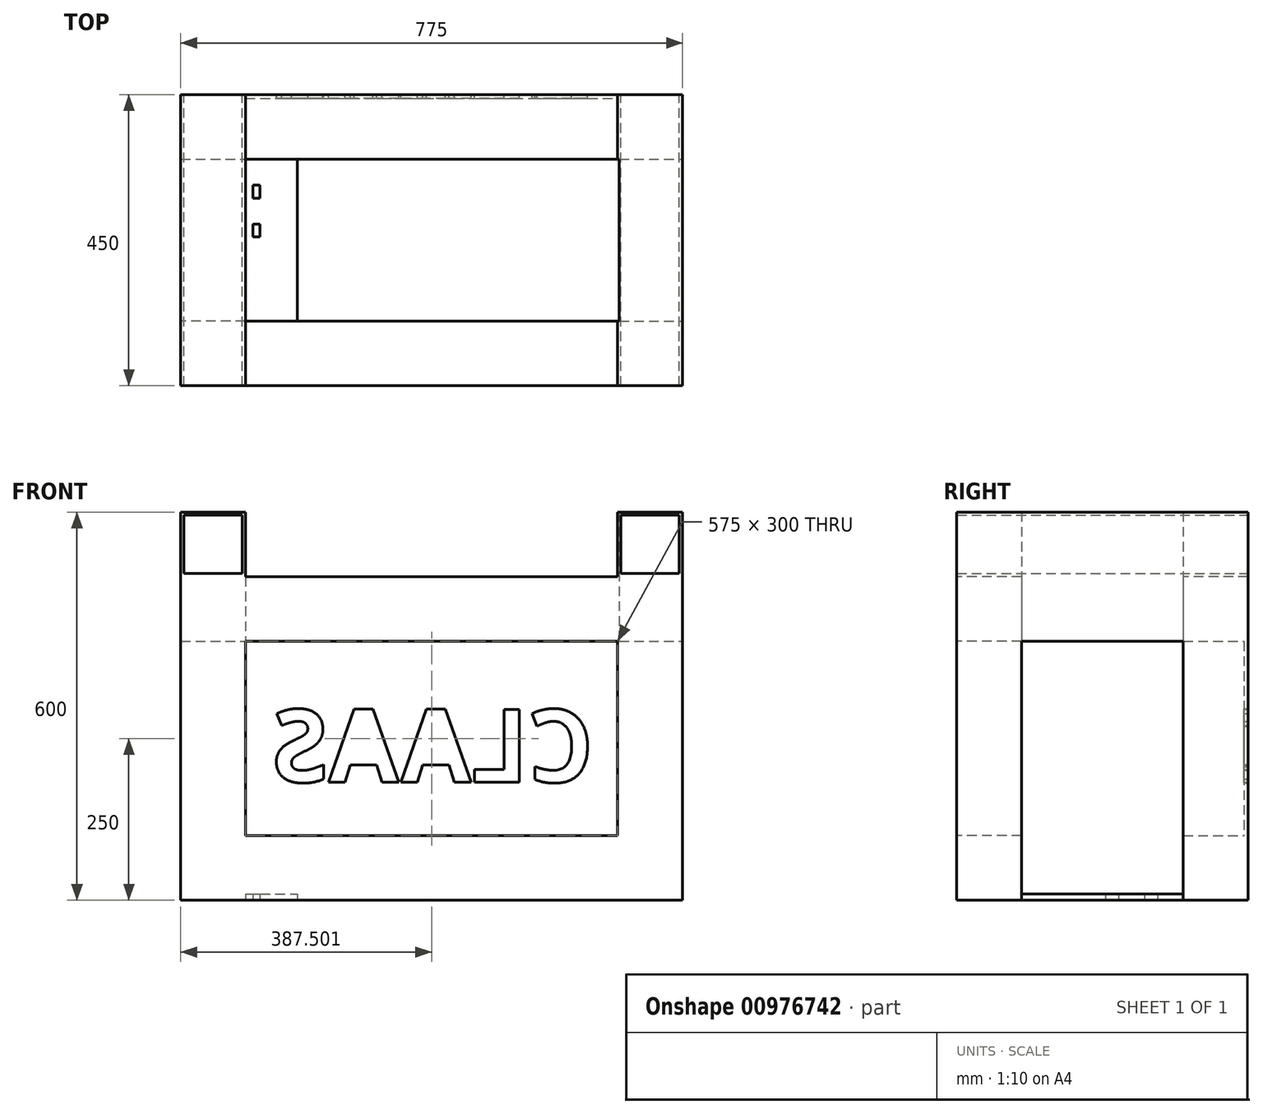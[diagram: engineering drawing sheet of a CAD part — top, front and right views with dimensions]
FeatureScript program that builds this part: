
annotation { "Feature Type Name" : "Feature", "Feature Type Description" : "" }
export const myFeature = defineFeature(function(context is Context, id is Id, definition is map)
    precondition{}
    {
        {
            var Q0;
            Q0=qCreatedBy(makeId("Top.planeOp"),FACE);
            var sketch = newSketch(context, id + "F0", { "sketchPlane" : qUnion([Q0])});
            skLineSegment(sketch, "E0.bottom", {"start": v(-50.26, -160.16) * mm, "end": v(724.74, -160.16) * mm});
            skLineSegment(sketch, "E0.top", {"start": v(-50.26, -260.16) * mm, "end": v(724.74, -260.16) * mm});
            skLineSegment(sketch, "E0.left", {"start": v(-50.26, -160.16) * mm, "end": v(-50.26, -260.16) * mm});
            skLineSegment(sketch, "E0.right", {"start": v(724.74, -160.16) * mm, "end": v(724.74, -260.16) * mm});
            skLineSegment(sketch, "E1.bottom", {"start": v(-50.26, -260.16) * mm, "end": v(49.74, -260.16) * mm});
            skLineSegment(sketch, "E1.top", {"start": v(-50.26, -510.16) * mm, "end": v(49.74, -510.16) * mm});
            skLineSegment(sketch, "E1.left", {"start": v(-50.26, -260.16) * mm, "end": v(-50.26, -510.16) * mm});
            skLineSegment(sketch, "E1.right", {"start": v(49.74, -260.16) * mm, "end": v(49.74, -510.16) * mm});
            skLineSegment(sketch, "E2.bottom", {"start": v(724.74, -260.16) * mm, "end": v(624.74, -260.16) * mm});
            skLineSegment(sketch, "E2.top", {"start": v(724.74, -510.16) * mm, "end": v(624.74, -510.16) * mm});
            skLineSegment(sketch, "E2.left", {"start": v(724.74, -260.16) * mm, "end": v(724.74, -510.16) * mm});
            skLineSegment(sketch, "E2.right", {"start": v(624.74, -260.16) * mm, "end": v(624.74, -510.16) * mm});
            skLineSegment(sketch, "E3.bottom", {"start": v(-50.26, -510.16) * mm, "end": v(724.74, -510.16) * mm});
            skLineSegment(sketch, "E3.top", {"start": v(-50.26, -610.16) * mm, "end": v(724.74, -610.16) * mm});
            skLineSegment(sketch, "E3.left", {"start": v(-50.26, -510.16) * mm, "end": v(-50.26, -610.16) * mm});
            skLineSegment(sketch, "E3.right", {"start": v(724.74, -510.16) * mm, "end": v(724.74, -610.16) * mm});
            skSolve(sketch);
        }
        {
            var Q0;
            Q0=makeQuery(id+"F0.imprint","IMPRINT",FACE,{"disambiguationData":[TD([[makeQuery(id+"F0.imprint","IMPRINT",EDGE,{"derivedFrom":sQuery(id+"F0.wireOp",EDGE,"E0.bottom")}),-1.0]])]});
            var Q1;
            Q1=makeQuery(id+"F0.imprint","IMPRINT",FACE,{"disambiguationData":[TD([[makeQuery(id+"F0.imprint","IMPRINT",EDGE,{"derivedFrom":sQuery(id+"F0.wireOp",EDGE,"E1.bottom")}),-1.0]])]});
            var Q2;
            Q2=makeQuery(id+"F0.imprint","IMPRINT",FACE,{"disambiguationData":[TD([[makeQuery(id+"F0.imprint","IMPRINT",EDGE,{"derivedFrom":sQuery(id+"F0.wireOp",EDGE,"E2.bottom")}),1.0]])]});
            var Q3;
            Q3=makeQuery(id+"F0.imprint","IMPRINT",FACE,{"disambiguationData":[TD([[makeQuery(id+"F0.imprint","IMPRINT",EDGE,{"derivedFrom":sQuery(id+"F0.wireOp",EDGE,"E3.top")}),1.0]])]});
            extrude(context, id + "F1", {"entities" : qUnion([Q0, Q1, Q2, Q3]), "depth" : 100 * mm, "offsetDistance" : 25 * mm});
        }
        {
            var Q0;
            Q0=makeQuery(id+"F1.opExtrude","CAP_FACE",FACE,{"disambiguationData":[OSD([sQuery(id+"F0.wireOp",EDGE,"E0.bottom"),sQuery(id+"F0.wireOp",EDGE,"E0.top"),sQuery(id+"F0.wireOp",EDGE,"E0.left"),sQuery(id+"F0.wireOp",EDGE,"E0.right"),sQuery(id+"F0.wireOp",EDGE,"E1.left"),sQuery(id+"F0.wireOp",EDGE,"E1.right"),sQuery(id+"F0.wireOp",EDGE,"E2.left"),sQuery(id+"F0.wireOp",EDGE,"E2.right"),sQuery(id+"F0.wireOp",EDGE,"E3.bottom"),sQuery(id+"F0.wireOp",EDGE,"E3.top"),sQuery(id+"F0.wireOp",EDGE,"E3.left"),sQuery(id+"F0.wireOp",EDGE,"E3.right")])],"isStart":false});
            var sketch = newSketch(context, id + "F2", { "sketchPlane" : qUnion([Q0])});
            skLineSegment(sketch, "E4.bottom", {"start": v(-50.26, -160.16) * mm, "end": v(49.74, -160.16) * mm});
            skLineSegment(sketch, "E4.top", {"start": v(-50.26, -260.16) * mm, "end": v(49.74, -260.16) * mm});
            skLineSegment(sketch, "E4.left", {"start": v(-50.26, -160.16) * mm, "end": v(-50.26, -260.16) * mm});
            skLineSegment(sketch, "E4.right", {"start": v(49.74, -160.16) * mm, "end": v(49.74, -260.16) * mm});
            skLineSegment(sketch, "E5.bottom", {"start": v(624.74, -260.16) * mm, "end": v(724.74, -260.16) * mm});
            skLineSegment(sketch, "E5.top", {"start": v(624.74, -160.16) * mm, "end": v(724.74, -160.16) * mm});
            skLineSegment(sketch, "E5.left", {"start": v(624.74, -260.16) * mm, "end": v(624.74, -160.16) * mm});
            skLineSegment(sketch, "E5.right", {"start": v(724.74, -260.16) * mm, "end": v(724.74, -160.16) * mm});
            skLineSegment(sketch, "E6.bottom", {"start": v(624.74, -510.16) * mm, "end": v(724.74, -510.16) * mm});
            skLineSegment(sketch, "E6.top", {"start": v(624.74, -610.16) * mm, "end": v(724.74, -610.16) * mm});
            skLineSegment(sketch, "E6.left", {"start": v(624.74, -510.16) * mm, "end": v(624.74, -610.16) * mm});
            skLineSegment(sketch, "E6.right", {"start": v(724.74, -510.16) * mm, "end": v(724.74, -610.16) * mm});
            skLineSegment(sketch, "E7.bottom", {"start": v(49.74, -510.16) * mm, "end": v(-50.26, -510.16) * mm});
            skLineSegment(sketch, "E7.top", {"start": v(49.74, -610.16) * mm, "end": v(-50.26, -610.16) * mm});
            skLineSegment(sketch, "E7.left", {"start": v(49.74, -510.16) * mm, "end": v(49.74, -610.16) * mm});
            skLineSegment(sketch, "E7.right", {"start": v(-50.26, -510.16) * mm, "end": v(-50.26, -610.16) * mm});
            skSolve(sketch);
        }
        {
            var Q0;
            Q0=makeQuery(id+"F2.imprint","IMPRINT",FACE,{"disambiguationData":[TD([[makeQuery(id+"F2.imprint","IMPRINT",EDGE,{"derivedFrom":sQuery(id+"F2.wireOp",EDGE,"E4.bottom")}),-1.0]])]});
            var Q1;
            Q1=makeQuery(id+"F2.imprint","IMPRINT",FACE,{"disambiguationData":[TD([[makeQuery(id+"F2.imprint","IMPRINT",EDGE,{"derivedFrom":sQuery(id+"F2.wireOp",EDGE,"E5.bottom")}),1.0]])]});
            var Q2;
            Q2=makeQuery(id+"F2.imprint","IMPRINT",FACE,{"disambiguationData":[TD([[makeQuery(id+"F2.imprint","IMPRINT",EDGE,{"derivedFrom":sQuery(id+"F2.wireOp",EDGE,"E6.bottom")}),-1.0]])]});
            var Q3;
            Q3=makeQuery(id+"F2.imprint","IMPRINT",FACE,{"disambiguationData":[TD([[makeQuery(id+"F2.imprint","IMPRINT",EDGE,{"derivedFrom":sQuery(id+"F2.wireOp",EDGE,"E7.bottom")}),1.0]])]});
            extrude(context, id + "F3", {"entities" : qUnion([Q0, Q1, Q2, Q3]), "operationType" : NewBodyOperationType.ADD, "depth" : 300 * mm, "offsetDistance" : 25 * mm});
        }
        {
            var Q0;
            Q0=makeQuery(id+"F3.opExtrude","CAP_FACE",FACE,{"disambiguationData":[OSD([sQuery(id+"F2.wireOp",EDGE,"E4.bottom"),sQuery(id+"F2.wireOp",EDGE,"E4.top"),sQuery(id+"F2.wireOp",EDGE,"E4.left"),sQuery(id+"F2.wireOp",EDGE,"E4.right")])],"isStart":false});
            var sketch = newSketch(context, id + "F4", { "sketchPlane" : qUnion([Q0])});
            skLineSegment(sketch, "E8.bottom", {"start": v(-50.26, -160.16) * mm, "end": v(724.74, -160.16) * mm});
            skLineSegment(sketch, "E8.top", {"start": v(-50.26, -260.16) * mm, "end": v(724.74, -260.16) * mm});
            skLineSegment(sketch, "E8.left", {"start": v(-50.26, -160.16) * mm, "end": v(-50.26, -260.16) * mm});
            skLineSegment(sketch, "E8.right", {"start": v(724.74, -160.16) * mm, "end": v(724.74, -260.16) * mm});
            skLineSegment(sketch, "E9.bottom", {"start": v(724.74, -260.16) * mm, "end": v(627.24, -260.16) * mm});
            skLineSegment(sketch, "E9.top", {"start": v(724.74, -510.16) * mm, "end": v(627.24, -510.16) * mm});
            skLineSegment(sketch, "E9.left", {"start": v(724.74, -260.16) * mm, "end": v(724.74, -510.16) * mm});
            skLineSegment(sketch, "E9.right", {"start": v(627.24, -260.16) * mm, "end": v(627.24, -510.16) * mm});
            skLineSegment(sketch, "E10.bottom", {"start": v(724.74, -510.16) * mm, "end": v(-50.26, -510.16) * mm});
            skLineSegment(sketch, "E10.top", {"start": v(724.74, -610.16) * mm, "end": v(-50.26, -610.16) * mm});
            skLineSegment(sketch, "E10.left", {"start": v(724.74, -510.16) * mm, "end": v(724.74, -610.16) * mm});
            skLineSegment(sketch, "E10.right", {"start": v(-50.26, -510.16) * mm, "end": v(-50.26, -610.16) * mm});
            skLineSegment(sketch, "E11.bottom", {"start": v(-50.26, -510.16) * mm, "end": v(49.74, -510.16) * mm});
            skLineSegment(sketch, "E11.top", {"start": v(-50.26, -260.16) * mm, "end": v(49.74, -260.16) * mm});
            skLineSegment(sketch, "E11.left", {"start": v(-50.26, -510.16) * mm, "end": v(-50.26, -260.16) * mm});
            skLineSegment(sketch, "E11.right", {"start": v(49.74, -510.16) * mm, "end": v(49.74, -260.16) * mm});
            skSolve(sketch);
        }
        {
            var Q0;
            Q0 = qSketchRegion(id + "F4", true);
            extrude(context, id + "F5", {"entities" : qUnion([Q0]), "operationType" : NewBodyOperationType.ADD, "depth" : 100 * mm, "offsetDistance" : 25 * mm});
        }
        {
            var Q0;
            Q0=makeQuery(id+"F1.opExtrude","CAP_FACE",FACE,{"disambiguationData":[OSD([sQuery(id+"F0.wireOp",EDGE,"E0.bottom"),sQuery(id+"F0.wireOp",EDGE,"E0.top"),sQuery(id+"F0.wireOp",EDGE,"E0.left"),sQuery(id+"F0.wireOp",EDGE,"E0.right"),sQuery(id+"F0.wireOp",EDGE,"E1.left"),sQuery(id+"F0.wireOp",EDGE,"E1.right"),sQuery(id+"F0.wireOp",EDGE,"E2.left"),sQuery(id+"F0.wireOp",EDGE,"E2.right"),sQuery(id+"F0.wireOp",EDGE,"E3.bottom"),sQuery(id+"F0.wireOp",EDGE,"E3.top"),sQuery(id+"F0.wireOp",EDGE,"E3.left"),sQuery(id+"F0.wireOp",EDGE,"E3.right")])],"isStart":true});
            var sketch = newSketch(context, id + "F6", { "sketchPlane" : qUnion([Q0])});
            skLineSegment(sketch, "E12.bottom", {"start": v(49.74, 510.16) * mm, "end": v(129.74, 510.16) * mm});
            skLineSegment(sketch, "E12.top", {"start": v(49.74, 260.16) * mm, "end": v(129.74, 260.16) * mm});
            skLineSegment(sketch, "E12.left", {"start": v(49.74, 510.16) * mm, "end": v(49.74, 260.16) * mm});
            skLineSegment(sketch, "E12.right", {"start": v(129.74, 510.16) * mm, "end": v(129.74, 260.16) * mm});
            skLineSegment(sketch, "E13.bottom", {"start": v(624.74, 510.16) * mm, "end": v(544.74, 510.16) * mm});
            skLineSegment(sketch, "E13.top", {"start": v(624.74, 260.16) * mm, "end": v(544.74, 260.16) * mm});
            skLineSegment(sketch, "E13.left", {"start": v(624.74, 510.16) * mm, "end": v(624.74, 260.16) * mm});
            skLineSegment(sketch, "E13.right", {"start": v(544.74, 510.16) * mm, "end": v(544.74, 260.16) * mm});
            skLineSegment(sketch, "E14.bottom", {"start": v(61.24, 300.16) * mm, "end": v(72.24, 300.16) * mm});
            skLineSegment(sketch, "E14.top", {"start": v(61.24, 320.16) * mm, "end": v(72.24, 320.16) * mm});
            skLineSegment(sketch, "E14.left", {"start": v(61.24, 300.16) * mm, "end": v(61.24, 320.16) * mm});
            skLineSegment(sketch, "E14.right", {"start": v(72.24, 300.16) * mm, "end": v(72.24, 320.16) * mm});
            skLineSegment(sketch, "E15.bottom", {"start": v(61.24, 360.16) * mm, "end": v(72.24, 360.16) * mm});
            skLineSegment(sketch, "E15.top", {"start": v(61.24, 380.16) * mm, "end": v(72.24, 380.16) * mm});
            skLineSegment(sketch, "E15.left", {"start": v(61.24, 360.16) * mm, "end": v(61.24, 380.16) * mm});
            skLineSegment(sketch, "E15.right", {"start": v(72.24, 360.16) * mm, "end": v(72.24, 380.16) * mm});
            skLineSegment(sketch, "E16.bottom", {"start": v(602.24, 380.16) * mm, "end": v(613.24, 380.16) * mm});
            skLineSegment(sketch, "E16.top", {"start": v(602.24, 360.16) * mm, "end": v(613.24, 360.16) * mm});
            skLineSegment(sketch, "E16.left", {"start": v(602.24, 380.16) * mm, "end": v(602.24, 360.16) * mm});
            skLineSegment(sketch, "E16.right", {"start": v(613.24, 380.16) * mm, "end": v(613.24, 360.16) * mm});
            skLineSegment(sketch, "E17.bottom", {"start": v(602.24, 320.16) * mm, "end": v(613.24, 320.16) * mm});
            skLineSegment(sketch, "E17.top", {"start": v(602.24, 300.16) * mm, "end": v(613.24, 300.16) * mm});
            skLineSegment(sketch, "E17.left", {"start": v(602.24, 320.16) * mm, "end": v(602.24, 300.16) * mm});
            skLineSegment(sketch, "E17.right", {"start": v(613.24, 320.16) * mm, "end": v(613.24, 300.16) * mm});
            skSolve(sketch);
        }
        {
            var Q0;
            Q0=makeQuery(id+"F6.imprint","IMPRINT",FACE,{"disambiguationData":[TD([[makeQuery(id+"F6.imprint","IMPRINT",EDGE,{"derivedFrom":sQuery(id+"F6.wireOp",EDGE,"E12.bottom")}),-1.0]])]});
            var Q1;
            Q1=makeQuery(id+"F6.imprint","IMPRINT",FACE,{"disambiguationData":[TD([[makeQuery(id+"F6.imprint","IMPRINT",EDGE,{"derivedFrom":sQuery(id+"F6.wireOp",EDGE,"E13.bottom")}),-1.0]])]});
            extrude(context, id + "F7", {"entities" : qUnion([Q0, Q1]), "oppositeDirection" : true, "depth" : 10 * mm, "offsetDistance" : 25 * mm});
        }
        {
            var Q0;
            Q0=makeQuery(id+"F5.boolean.opBoolean","MERGE",FACE,{"derivedFrom":[makeQuery(id+"F3.boolean.opBoolean","MERGE",FACE,{"derivedFrom":[makeQuery(id+"F1.opExtrude","SWEPT_FACE",FACE,{"disambiguationData":[OSD([sQuery(id+"F0.wireOp",EDGE,"E0.bottom")])]}),makeQuery(id+"F3.opExtrude","SWEPT_FACE",FACE,{"disambiguationData":[OSD([sQuery(id+"F2.wireOp",EDGE,"E4.bottom")])]}),makeQuery(id+"F3.opExtrude","SWEPT_FACE",FACE,{"disambiguationData":[OSD([sQuery(id+"F2.wireOp",EDGE,"E5.top")])]})]}),makeQuery(id+"F5.opExtrude","SWEPT_FACE",FACE,{"disambiguationData":[OSD([sQuery(id+"F4.wireOp",EDGE,"E8.bottom")])]})]});
            var sketch = newSketch(context, id + "F8", { "sketchPlane" : qUnion([Q0])});
            skLineSegment(sketch, "E18.bottom", {"start": v(-49.74, 100) * mm, "end": v(-624.74, 100) * mm});
            skLineSegment(sketch, "E18.top", {"start": v(-49.74, 400) * mm, "end": v(-624.74, 400) * mm});
            skLineSegment(sketch, "E18.left", {"start": v(-49.74, 100) * mm, "end": v(-49.74, 400) * mm});
            skLineSegment(sketch, "E18.right", {"start": v(-624.74, 100) * mm, "end": v(-624.74, 400) * mm});
            skText(sketch, "E19", { "text": "CLAAS", "fontName": "NotoSans-Bold.ttf"});
            const initialGuessF8  = {"E19": [-0.58724, 0.1825, 1, 0, 0.11322]};
            skSetInitialGuess(sketch, initialGuessF8);
            skSolve(sketch);
        }
        {
            var Q0;
            Q0 = qSketchRegion(id + "F8", true);
            extrude(context, id + "F9", {"entities" : qUnion([Q0]), "operationType" : NewBodyOperationType.ADD, "oppositeDirection" : true, "depth" : 6 * mm, "offsetDistance" : 25 * mm});
        }
        {
            var Q0;
            Q0=makeQuery(id+"F5.opExtrude","CAP_FACE",FACE,{"disambiguationData":[OSD([sQuery(id+"F4.wireOp",EDGE,"E8.bottom"),sQuery(id+"F4.wireOp",EDGE,"E8.top"),sQuery(id+"F4.wireOp",EDGE,"E8.left"),sQuery(id+"F4.wireOp",EDGE,"E8.right"),sQuery(id+"F4.wireOp",EDGE,"E9.left"),sQuery(id+"F4.wireOp",EDGE,"E9.right"),sQuery(id+"F4.wireOp",EDGE,"E10.bottom"),sQuery(id+"F4.wireOp",EDGE,"E10.top"),sQuery(id+"F4.wireOp",EDGE,"E10.left"),sQuery(id+"F4.wireOp",EDGE,"E10.right"),sQuery(id+"F4.wireOp",EDGE,"E11.left"),sQuery(id+"F4.wireOp",EDGE,"E11.right")])],"isStart":false});
            var sketch = newSketch(context, id + "F10", { "sketchPlane" : qUnion([Q0])});
            skLineSegment(sketch, "E20.bottom", {"start": v(-50.26, -160.16) * mm, "end": v(49.74, -160.16) * mm});
            skLineSegment(sketch, "E20.top", {"start": v(-50.26, -610.16) * mm, "end": v(49.74, -610.16) * mm});
            skLineSegment(sketch, "E20.left", {"start": v(-50.26, -160.16) * mm, "end": v(-50.26, -610.16) * mm});
            skLineSegment(sketch, "E20.right", {"start": v(49.74, -160.16) * mm, "end": v(49.74, -610.16) * mm});
            skLineSegment(sketch, "E21.bottom", {"start": v(724.74, -160.16) * mm, "end": v(624.74, -160.16) * mm});
            skLineSegment(sketch, "E21.top", {"start": v(724.74, -610.16) * mm, "end": v(624.74, -610.16) * mm});
            skLineSegment(sketch, "E21.left", {"start": v(724.74, -160.16) * mm, "end": v(724.74, -610.16) * mm});
            skLineSegment(sketch, "E21.right", {"start": v(624.74, -160.16) * mm, "end": v(624.74, -610.16) * mm});
            skSolve(sketch);
        }
        {
            var Q0;
            {var subQ2=sQuery(id+"F10.wireOp",EDGE,"E20.bottom");Q0=makeQuery(id+"F10.imprint","IMPRINT",FACE,{"disambiguationData":[TD([[makeQuery(id+"F10.imprint","IMPRINT",EDGE,{"derivedFrom":subQ2}),-1.0]])]});}
            var Q1;
            {var subQ1=sQuery(id+"F10.wireOp",EDGE,"E21.bottom");Q1=makeQuery(id+"F10.imprint","IMPRINT",FACE,{"disambiguationData":[TD([[makeQuery(id+"F10.imprint","IMPRINT",EDGE,{"derivedFrom":subQ1}),-1.0]])]});}
            extrude(context, id + "F11", {"entities" : qUnion([Q0, Q1]), "operationType" : NewBodyOperationType.ADD, "depth" : 100 * mm, "offsetDistance" : 25 * mm});
        }
        {
            var Q0;
            Q0=makeQuery(id+"F11.boolean.opBoolean","MERGE",FACE,{"derivedFrom":[makeQuery(id+"F9.boolean.opBoolean","MERGE",FACE,{"derivedFrom":[makeQuery(id+"F5.boolean.opBoolean","MERGE",FACE,{"derivedFrom":[makeQuery(id+"F3.boolean.opBoolean","MERGE",FACE,{"derivedFrom":[makeQuery(id+"F1.opExtrude","SWEPT_FACE",FACE,{"disambiguationData":[OSD([sQuery(id+"F0.wireOp",EDGE,"E0.bottom")])]}),makeQuery(id+"F3.opExtrude","SWEPT_FACE",FACE,{"disambiguationData":[OSD([sQuery(id+"F2.wireOp",EDGE,"E4.bottom")])]}),makeQuery(id+"F3.opExtrude","SWEPT_FACE",FACE,{"disambiguationData":[OSD([sQuery(id+"F2.wireOp",EDGE,"E5.top")])]})]}),makeQuery(id+"F5.opExtrude","SWEPT_FACE",FACE,{"disambiguationData":[OSD([sQuery(id+"F4.wireOp",EDGE,"E8.bottom")])]})]}),makeQuery(id+"F9.opExtrude","CAP_FACE",FACE,{"disambiguationData":[OSD([sQuery(id+"F8.wireOp",EDGE,"E18.bottom"),sQuery(id+"F8.wireOp",EDGE,"E18.top"),sQuery(id+"F8.wireOp",EDGE,"E18.left"),sQuery(id+"F8.wireOp",EDGE,"E18.right"),sQuery(id+"F8.wireOp",EDGE,"E19.sketch_text.stroke-0"),sQuery(id+"F8.wireOp",EDGE,"E19.sketch_text.stroke-1"),sQuery(id+"F8.wireOp",EDGE,"E19.sketch_text.stroke-2"),sQuery(id+"F8.wireOp",EDGE,"E19.sketch_text.stroke-3"),sQuery(id+"F8.wireOp",EDGE,"E19.sketch_text.stroke-4"),sQuery(id+"F8.wireOp",EDGE,"E19.sketch_text.stroke-5"),sQuery(id+"F8.wireOp",EDGE,"E19.sketch_text.stroke-6"),sQuery(id+"F8.wireOp",EDGE,"E19.sketch_text.stroke-7"),sQuery(id+"F8.wireOp",EDGE,"E19.sketch_text.stroke-8"),sQuery(id+"F8.wireOp",EDGE,"E19.sketch_text.stroke-9"),sQuery(id+"F8.wireOp",EDGE,"E19.sketch_text.stroke-10"),sQuery(id+"F8.wireOp",EDGE,"E19.sketch_text.stroke-11"),sQuery(id+"F8.wireOp",EDGE,"E19.sketch_text.stroke-12"),sQuery(id+"F8.wireOp",EDGE,"E19.sketch_text.stroke-13"),sQuery(id+"F8.wireOp",EDGE,"E19.sketch_text.stroke-14"),sQuery(id+"F8.wireOp",EDGE,"E19.sketch_text.stroke-15"),sQuery(id+"F8.wireOp",EDGE,"E19.sketch_text.stroke-16"),sQuery(id+"F8.wireOp",EDGE,"E19.sketch_text.stroke-17"),sQuery(id+"F8.wireOp",EDGE,"E19.sketch_text.stroke-18"),sQuery(id+"F8.wireOp",EDGE,"E19.sketch_text.stroke-19"),sQuery(id+"F8.wireOp",EDGE,"E19.sketch_text.stroke-20"),sQuery(id+"F8.wireOp",EDGE,"E19.sketch_text.stroke-21"),sQuery(id+"F8.wireOp",EDGE,"E19.sketch_text.stroke-22"),sQuery(id+"F8.wireOp",EDGE,"E19.sketch_text.stroke-23"),sQuery(id+"F8.wireOp",EDGE,"E19.sketch_text.stroke-24"),sQuery(id+"F8.wireOp",EDGE,"E19.sketch_text.stroke-25"),sQuery(id+"F8.wireOp",EDGE,"E19.sketch_text.stroke-26"),sQuery(id+"F8.wireOp",EDGE,"E19.sketch_text.stroke-27"),sQuery(id+"F8.wireOp",EDGE,"E19.sketch_text.stroke-28"),sQuery(id+"F8.wireOp",EDGE,"E19.sketch_text.stroke-33"),sQuery(id+"F8.wireOp",EDGE,"E19.sketch_text.stroke-34"),sQuery(id+"F8.wireOp",EDGE,"E19.sketch_text.stroke-35"),sQuery(id+"F8.wireOp",EDGE,"E19.sketch_text.stroke-36"),sQuery(id+"F8.wireOp",EDGE,"E19.sketch_text.stroke-37"),sQuery(id+"F8.wireOp",EDGE,"E19.sketch_text.stroke-38"),sQuery(id+"F8.wireOp",EDGE,"E19.sketch_text.stroke-39"),sQuery(id+"F8.wireOp",EDGE,"E19.sketch_text.stroke-40"),sQuery(id+"F8.wireOp",EDGE,"E19.sketch_text.stroke-45"),sQuery(id+"F8.wireOp",EDGE,"E19.sketch_text.stroke-46"),sQuery(id+"F8.wireOp",EDGE,"E19.sketch_text.stroke-47"),sQuery(id+"F8.wireOp",EDGE,"E19.sketch_text.stroke-48"),sQuery(id+"F8.wireOp",EDGE,"E19.sketch_text.stroke-49"),sQuery(id+"F8.wireOp",EDGE,"E19.sketch_text.stroke-50"),sQuery(id+"F8.wireOp",EDGE,"E19.sketch_text.stroke-51"),sQuery(id+"F8.wireOp",EDGE,"E19.sketch_text.stroke-52"),sQuery(id+"F8.wireOp",EDGE,"E19.sketch_text.stroke-53"),sQuery(id+"F8.wireOp",EDGE,"E19.sketch_text.stroke-54"),sQuery(id+"F8.wireOp",EDGE,"E19.sketch_text.stroke-55"),sQuery(id+"F8.wireOp",EDGE,"E19.sketch_text.stroke-56"),sQuery(id+"F8.wireOp",EDGE,"E19.sketch_text.stroke-57"),sQuery(id+"F8.wireOp",EDGE,"E19.sketch_text.stroke-58"),sQuery(id+"F8.wireOp",EDGE,"E19.sketch_text.stroke-59"),sQuery(id+"F8.wireOp",EDGE,"E19.sketch_text.stroke-60"),sQuery(id+"F8.wireOp",EDGE,"E19.sketch_text.stroke-61"),sQuery(id+"F8.wireOp",EDGE,"E19.sketch_text.stroke-62"),sQuery(id+"F8.wireOp",EDGE,"E19.sketch_text.stroke-63"),sQuery(id+"F8.wireOp",EDGE,"E19.sketch_text.stroke-64"),sQuery(id+"F8.wireOp",EDGE,"E19.sketch_text.stroke-65"),sQuery(id+"F8.wireOp",EDGE,"E19.sketch_text.stroke-66"),sQuery(id+"F8.wireOp",EDGE,"E19.sketch_text.stroke-67"),sQuery(id+"F8.wireOp",EDGE,"E19.sketch_text.stroke-68"),sQuery(id+"F8.wireOp",EDGE,"E19.sketch_text.stroke-69"),sQuery(id+"F8.wireOp",EDGE,"E19.sketch_text.stroke-70"),sQuery(id+"F8.wireOp",EDGE,"E19.sketch_text.stroke-71"),sQuery(id+"F8.wireOp",EDGE,"E19.sketch_text.stroke-72")])],"isStart":true})]}),makeQuery(id+"F11.opExtrude","SWEPT_FACE",FACE,{"disambiguationData":[OSD([sQuery(id+"F10.wireOp",EDGE,"E20.bottom")])]}),makeQuery(id+"F11.opExtrude","SWEPT_FACE",FACE,{"disambiguationData":[OSD([sQuery(id+"F10.wireOp",EDGE,"E21.bottom")])]})]});
            var sketch = newSketch(context, id + "F12", { "sketchPlane" : qUnion([Q0])});
            skLineSegment(sketch, "E22.bottom", {"start": v(45.26, 505) * mm, "end": v(-44.74, 505) * mm});
            skLineSegment(sketch, "E22.top", {"start": v(45.26, 595) * mm, "end": v(-44.74, 595) * mm});
            skLineSegment(sketch, "E22.left", {"start": v(45.26, 505) * mm, "end": v(45.26, 595) * mm});
            skLineSegment(sketch, "E22.right", {"start": v(-44.74, 505) * mm, "end": v(-44.74, 595) * mm});
            skLineSegment(sketch, "E23.bottom", {"start": v(-629.74, 505) * mm, "end": v(-719.74, 505) * mm});
            skLineSegment(sketch, "E23.top", {"start": v(-629.74, 595) * mm, "end": v(-719.74, 595) * mm});
            skLineSegment(sketch, "E23.left", {"start": v(-629.74, 505) * mm, "end": v(-629.74, 595) * mm});
            skLineSegment(sketch, "E23.right", {"start": v(-719.74, 505) * mm, "end": v(-719.74, 595) * mm});
            skSolve(sketch);
        }
        {
            var Q0;
            Q0=makeQuery(id+"F12.imprint","IMPRINT",FACE,{"disambiguationData":[TD([[makeQuery(id+"F12.imprint","IMPRINT",EDGE,{"derivedFrom":sQuery(id+"F12.wireOp",EDGE,"E23.bottom")}),-1.0]])]});
            var Q1;
            Q1=makeQuery(id+"F12.imprint","IMPRINT",FACE,{"disambiguationData":[TD([[makeQuery(id+"F12.imprint","IMPRINT",EDGE,{"derivedFrom":sQuery(id+"F12.wireOp",EDGE,"E22.bottom")}),-1.0]])]});
            extrude(context, id + "F13", {"entities" : qUnion([Q0, Q1]), "operationType" : NewBodyOperationType.REMOVE, "oppositeDirection" : true, "depth" : 450 * mm, "offsetDistance" : 25 * mm});
        }
    });
